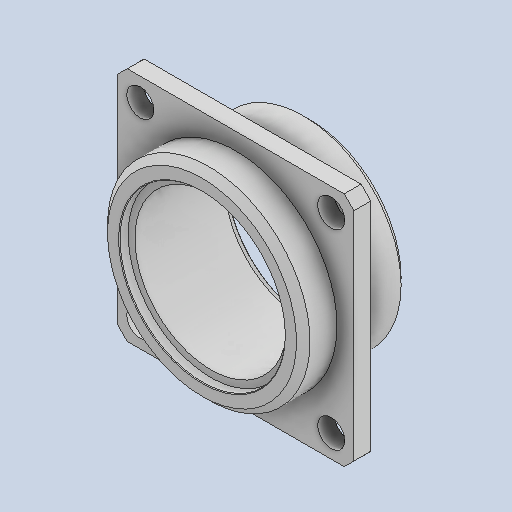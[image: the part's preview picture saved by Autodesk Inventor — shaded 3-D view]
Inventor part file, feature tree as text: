
AUTODESK INVENTOR PART (.ipt)
format: ipt  version: 2023 (Build 270158030, 158C)  size: 171,008 bytes
history: native  units: in
note: dims shown in document units (in); Inventor stores cm internally (conversion verified against a paired STEP export)
features: fillet x1
ambient origin geometry x8: Origin, YZ Plane, XZ Plane, XY Plane, X Axis, Y Axis, Z Axis, Center Point
bodies: Solid1 (feature_tree)
feature tree (1):
  fillet  "Fillet2"  [1 undecoded]
note: 1 required parameter value undecoded (feature->parameter linkage not recoverable at this tier; creation-order binding heuristic only, values carry confidence <= 0.55)
